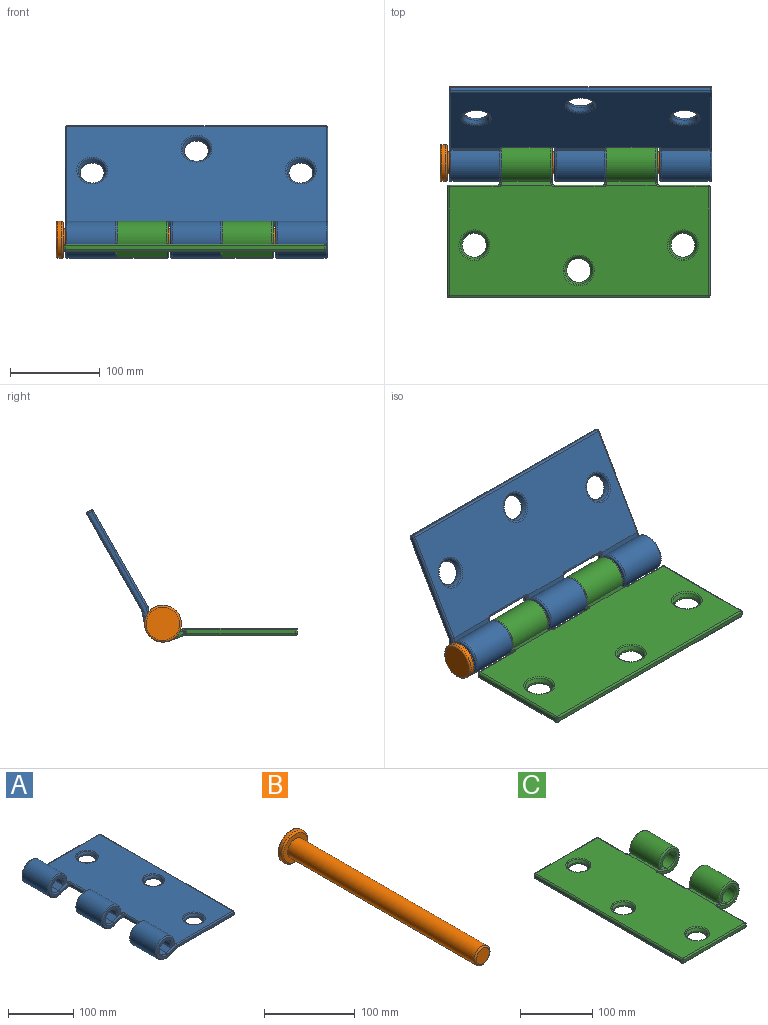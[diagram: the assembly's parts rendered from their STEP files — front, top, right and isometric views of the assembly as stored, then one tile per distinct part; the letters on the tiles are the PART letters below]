
ASSEMBLY  parts=3 mates=2
PART A: 101 faces, bbox 171.7x292x44.4 mm
  f0: cylinder r=12.5mm len=54.4mm, axis (0,1,0), area 3703.3mm2, adj f2,f8,f36,f85
  f1: cylinder r=12.5mm len=54.4mm, axis (0,1,0), area 3703.3mm2, adj f3,f9,f45,f56
  f2: plane 55.3x20.54mm, normal (-0.32,0,0.95), area 1179mm2, adj f0,f12,f33,f34,f35,f80
  f3: plane 56.21x20.54mm, normal (-0.32,0,0.95), area 1179.8mm2, adj f1,f12,f39,f41,f43,f53,f54,f55
  f4: plane 54.63x17.59mm, normal (0.34,0,-0.94), area 1016.4mm2, adj f6,f14,f42,f44,f93
  f5: plane 54.85x17.59mm, normal (0.34,0,-0.94), area 1016.5mm2, adj f7,f14,f51,f52,f62,f64
  f6: cylinder r=20.5mm len=54.4mm, axis (0,1,0), area 5913.6mm2, adj f4,f8,f40,f91
  f7: cylinder r=20.5mm len=54.4mm, axis (0,1,0), area 5913.6mm2, adj f5,f9,f49,f60
  f8: plane 54.4x8.42mm, normal (0,0,-1), area 458.3mm2, adj f0,f6,f38,f88
  f9: plane 54.4x8.42mm, normal (0,0,-1), area 458.3mm2, adj f1,f7,f47,f58
  f10: cylinder r=12.5mm len=54.4mm, axis (0,1,0), area 3703.3mm2, adj f11,f17,f65,f73
  f11: plane 55.3x20.54mm, normal (-0.32,0,0.95), area 1179mm2, adj f10,f12,f59,f61,f63,f74
  f12: plane 288x123mm, normal (0,0,1), area 32386.8mm2, adj f2,f3,f11,f35,f37,f39,f55,f57
  f13: plane 288x4mm, normal (1,0,0), area 1152mm2, adj f82,f83,f89,f90
  f14: plane 288x123.06mm, normal (0,0,-1), area 32998.9mm2, adj f4,f5,f15,f44,f46,f48,f50,f52
  f15: plane 54.63x17.59mm, normal (0.34,0,-0.94), area 1016.4mm2, adj f14,f16,f71,f72,f79
  f16: cylinder r=20.5mm len=54.4mm, axis (0,1,0), area 5913.6mm2, adj f15,f17,f69,f77
  f17: plane 54.4x8.42mm, normal (0,0,-1), area 458.3mm2, adj f10,f16,f67,f75
  f18: plane 166x37mm, normal (0,-1,0), area 913.5mm2, adj f80,f81,f85,f88,f89,f91,f93,f94
  f19: plane 166x37mm, normal (0,1,0), area 913.5mm2, adj f73,f74,f75,f76,f77,f79,f83,f84
  f20: cone r=16mm half-angle=26.6deg, axis (0,0,1), area 406mm2, adj f99,f100
  f21: cone r=12mm half-angle=26.6deg, axis (0,0,1), area 406mm2, adj f97,f98
  f22: cone r=16mm half-angle=26.6deg, axis (0,0,1), area 406mm2, adj f95,f96
  f23: plane 54.4x4mm, normal (-1,0,0), area 217.6mm2, adj f29,f30,f57,f68
  f24: plane 41x37mm, normal (0,1,0), area 413.9mm2, adj f29,f54,f56,f58,f60,f62
  f25: plane 41x37mm, normal (0,-1,0), area 413.9mm2, adj f30,f63,f65,f67,f69,f71
  f26: plane 54.4x4mm, normal (-1,0,0), area 217.6mm2, adj f31,f32,f37,f48
  f27: plane 41x37mm, normal (0,1,0), area 413.9mm2, adj f31,f34,f36,f38,f40,f42
  f28: plane 41x37mm, normal (0,-1,0), area 413.9mm2, adj f32,f43,f45,f47,f49,f51
  f29: cylinder r=2mm len=4.59mm, axis (0,0,1), area 12.3mm2, adj f23,f24,f53,f55,f64,f66
  f30: cylinder r=2mm len=4.59mm, axis (0,0,-1), area 12.3mm2, adj f23,f25,f59,f61,f70,f72
  f31: cylinder r=2mm len=4.59mm, axis (0,0,1), area 12.3mm2, adj f26,f27,f33,f35,f44,f46
  f32: cylinder r=2mm len=4.59mm, axis (0,0,-1), area 12.3mm2, adj f26,f28,f39,f41,f50,f52
  f33: bspline ~2.75x2.54mm, area 6mm2, adj f2,f31,f34,f35
  f34: cylinder r=2mm len=18.54mm, axis (-0.95,0,-0.32), area 59.3mm2, adj f2,f27,f33,f36
  f35: torus R=4mm, axis (0,0,-1), area 8.7mm2, adj f2,f12,f31,f33,f37
  f36: torus R=14.5mm, axis (0,1,0), area 222mm2, adj f0,f27,f34,f38
  f37: cylinder r=2mm len=54.4mm, axis (0,-1,0), area 170.9mm2, adj f12,f26,f35,f39
  f38: cylinder r=2mm len=8.42mm, axis (1,0,0), area 19.6mm2, adj f8,f27,f36,f40
  f39: torus R=4mm, axis (0,0,-1), area 8.7mm2, adj f3,f12,f32,f37,f41
  f40: torus R=18.5mm, axis (0,1,0), area 326.9mm2, adj f6,f27,f38,f42
  f41: bspline ~3.65x3.11mm, area 6mm2, adj f3,f32,f39,f43
  f42: cylinder r=2mm len=16.94mm, axis (0.94,0,0.34), area 54.3mm2, adj f4,f27,f40,f44
  f43: cylinder r=2mm len=18.54mm, axis (0.95,0,0.32), area 59.3mm2, adj f3,f28,f41,f45
  f44: bspline ~2.47x2.33mm, area 3.5mm2, adj f4,f14,f31,f42,f46
  f45: torus R=14.5mm, axis (0,1,0), area 222mm2, adj f1,f28,f43,f47
  f46: torus R=4mm, axis (0,0,1), area 9.2mm2, adj f14,f31,f44,f48
  f47: cylinder r=2mm len=8.42mm, axis (-1,0,0), area 19.6mm2, adj f9,f28,f45,f49
  f48: cylinder r=2mm len=54.4mm, axis (0,1,0), area 170.9mm2, adj f14,f26,f46,f50
  f49: torus R=18.5mm, axis (0,1,0), area 326.9mm2, adj f7,f28,f47,f51
  f50: torus R=4mm, axis (0,0,1), area 9.2mm2, adj f14,f32,f48,f52
  f51: cylinder r=2mm len=16.94mm, axis (-0.94,0,-0.34), area 54.3mm2, adj f5,f28,f49,f52
  f52: bspline ~2.47x2.33mm, area 3.5mm2, adj f5,f14,f32,f50,f51
  f53: bspline ~2.75x2.54mm, area 6mm2, adj f3,f29,f54,f55
  f54: cylinder r=2mm len=18.54mm, axis (-0.95,0,-0.32), area 59.3mm2, adj f3,f24,f53,f56
  f55: torus R=4mm, axis (0,0,-1), area 8.7mm2, adj f3,f12,f29,f53,f57
  f56: torus R=14.5mm, axis (0,1,0), area 222mm2, adj f1,f24,f54,f58
  f57: cylinder r=2mm len=54.4mm, axis (0,-1,0), area 170.9mm2, adj f12,f23,f55,f59
  f58: cylinder r=2mm len=8.42mm, axis (1,0,0), area 19.6mm2, adj f9,f24,f56,f60
  f59: torus R=4mm, axis (0,0,-1), area 8.7mm2, adj f11,f12,f30,f57,f61
  f60: torus R=18.5mm, axis (0,1,0), area 326.9mm2, adj f7,f24,f58,f62
  f61: bspline ~3.65x3.11mm, area 6mm2, adj f11,f30,f59,f63
  f62: cylinder r=2mm len=16.94mm, axis (0.94,0,0.34), area 54.3mm2, adj f5,f24,f60,f64
  f63: cylinder r=2mm len=18.54mm, axis (0.95,0,0.32), area 59.3mm2, adj f11,f25,f61,f65
  f64: bspline ~2.47x2.33mm, area 3.5mm2, adj f5,f14,f29,f62,f66
  f65: torus R=14.5mm, axis (0,1,0), area 222mm2, adj f10,f25,f63,f67
  f66: torus R=4mm, axis (0,0,1), area 9.2mm2, adj f14,f29,f64,f68
  f67: cylinder r=2mm len=8.42mm, axis (-1,0,0), area 19.6mm2, adj f17,f25,f65,f69
  f68: cylinder r=2mm len=54.4mm, axis (0,1,0), area 170.9mm2, adj f14,f23,f66,f70
  f69: torus R=18.5mm, axis (0,1,0), area 326.9mm2, adj f16,f25,f67,f71
  f70: torus R=4mm, axis (0,0,1), area 9.2mm2, adj f14,f30,f68,f72
  f71: cylinder r=2mm len=16.94mm, axis (-0.94,0,-0.34), area 54.3mm2, adj f15,f25,f69,f72
  f72: bspline ~2.47x2.33mm, area 3.5mm2, adj f14,f15,f30,f70,f71
  f73: torus R=14.5mm, axis (0,-1,0), area 222mm2, adj f10,f19,f74,f75
  f74: cylinder r=2mm len=21.18mm, axis (0.95,0,0.32), area 67.5mm2, adj f11,f19,f73,f76
  f75: cylinder r=2mm len=8.42mm, axis (-1,0,0), area 19.6mm2, adj f17,f19,f73,f77
  f76: cylinder r=2mm len=123mm, axis (1,0,0), area 385.9mm2, adj f12,f19,f74,f78
  f77: torus R=18.5mm, axis (0,-1,0), area 326.9mm2, adj f16,f19,f75,f79
  f78: sphere r=2mm, area 6.3mm2, adj f76,f82,f83
  f79: cylinder r=2mm len=18.59mm, axis (-0.94,0,-0.34), area 59.2mm2, adj f15,f19,f77,f84
  f80: cylinder r=2mm len=21.18mm, axis (-0.95,0,-0.32), area 67.5mm2, adj f2,f18,f81,f85
  f81: cylinder r=2mm len=123mm, axis (-1,0,0), area 385.9mm2, adj f12,f18,f80,f86
  f82: cylinder r=2mm len=288mm, axis (0,1,0), area 904.8mm2, adj f12,f13,f78,f86
  f83: cylinder r=2mm len=4mm, axis (0,0,-1), area 12.6mm2, adj f13,f19,f78,f87
  f84: cylinder r=2mm len=123.35mm, axis (-1,0,0), area 387mm2, adj f14,f19,f79,f87
  f85: torus R=14.5mm, axis (0,-1,0), area 222mm2, adj f0,f18,f80,f88
  f86: sphere r=2mm, area 6.3mm2, adj f81,f82,f89
  f87: sphere r=2mm, area 4mm2, adj f83,f84,f90
  f88: cylinder r=2mm len=8.42mm, axis (1,0,0), area 19.6mm2, adj f8,f18,f85,f91
  f89: cylinder r=2mm len=4mm, axis (0,0,1), area 12.6mm2, adj f13,f18,f86,f92
  f90: cylinder r=2mm len=288mm, axis (0,1,0), area 904.8mm2, adj f13,f14,f87,f92
  f91: torus R=18.5mm, axis (0,-1,0), area 326.9mm2, adj f6,f18,f88,f93
  f92: sphere r=2mm, area 6.3mm2, adj f89,f90,f94
  f93: cylinder r=2mm len=18.59mm, axis (0.94,0,0.34), area 59.2mm2, adj f4,f18,f91,f94
  f94: cylinder r=2mm len=123.35mm, axis (1,0,0), area 387mm2, adj f14,f18,f92,f93
  f95: torus R=17.24mm, axis (0,0,-1), area 225.9mm2, adj f12,f22
  f96: torus R=15.24mm, axis (0,0,1), area 353.1mm2, adj f14,f22
  f97: torus R=15.24mm, axis (0,0,1), area 353.1mm2, adj f14,f21
  f98: torus R=17.24mm, axis (0,0,-1), area 225.9mm2, adj f12,f21
  f99: torus R=15.24mm, axis (0,0,1), area 353.1mm2, adj f14,f20
  f100: torus R=17.24mm, axis (0,0,-1), area 225.9mm2, adj f12,f20
PART B: 8 faces, bbox 44.4x300x44.4 mm
  f0: cylinder r=12.25mm len=290mm, axis (0,1,0), area 22321mm2, adj f4,f7
  f1: plane 20.5x20.5mm, normal (0,-1,0), area 330.1mm2, adj f7
  f2: cylinder r=20.5mm len=41mm, axis (0,-1,0), area 515.2mm2, adj f5,f6
  f3: plane 37x37mm, normal (0,1,0), area 1075.2mm2, adj f6
  f4: plane 37x37mm, normal (0,-1,0), area 603.8mm2, adj f0,f5
  f5: torus R=18.5mm, axis (0,1,0), area 390.3mm2, adj f2,f4
  f6: torus R=18.5mm, axis (0,1,0), area 390.3mm2, adj f2,f3
  f7: torus R=10.25mm, axis (0,1,0), area 227.5mm2, adj f0,f1
PART C: 95 faces, bbox 171.7x292x44.4 mm
  f0: cylinder r=12.5mm len=54.4mm, axis (0,1,0), area 3703.3mm2, adj f2,f8,f36,f60
  f1: cylinder r=12.5mm len=54.4mm, axis (0,1,0), area 3703.3mm2, adj f3,f9,f53,f69
  f2: plane 56.21x20.54mm, normal (0.32,0,0.95), area 1179.8mm2, adj f0,f12,f38,f40,f42,f57,f58,f59
  f3: plane 56.21x20.54mm, normal (0.32,0,0.95), area 1179.8mm2, adj f1,f12,f54,f55,f56,f63,f65,f67
  f4: plane 54.85x17.59mm, normal (-0.34,0,-0.94), area 1016.5mm2, adj f6,f14,f29,f30,f66,f68
  f5: plane 54.85x17.59mm, normal (-0.34,0,-0.94), area 1016.5mm2, adj f7,f14,f45,f47,f75,f76
  f6: cylinder r=20.5mm len=54.4mm, axis (0,1,0), area 5913.6mm2, adj f4,f8,f32,f64
  f7: cylinder r=20.5mm len=54.4mm, axis (0,1,0), area 5913.6mm2, adj f5,f9,f49,f73
  f8: plane 54.4x8.42mm, normal (0,0,-1), area 458.3mm2, adj f0,f6,f34,f62
  f9: plane 54.4x8.42mm, normal (0,0,-1), area 458.3mm2, adj f1,f7,f51,f71
  f10: plane 121x4mm, normal (0,-1,0), area 484mm2, adj f39,f50,f78,f84
  f11: plane 121x4mm, normal (0,1,0), area 484mm2, adj f35,f46,f81,f87
  f12: plane 288x123mm, normal (0,0,1), area 32278mm2, adj f2,f3,f42,f44,f46,f48,f50,f52
  f13: plane 288x4mm, normal (-1,0,0), area 1152mm2, adj f37,f48,f78,f81
  f14: plane 288x123.06mm, normal (0,0,-1), area 32890.1mm2, adj f4,f5,f29,f31,f33,f35,f37,f39
  f15: cone r=16mm half-angle=26.6deg, axis (0,0,1), area 406mm2, adj f93,f94
  f16: cone r=12mm half-angle=26.6deg, axis (0,0,1), area 406mm2, adj f91,f92
  f17: cone r=16mm half-angle=26.6deg, axis (0,0,1), area 406mm2, adj f89,f90
  f18: plane 54.4x4mm, normal (1,0,0), area 217.6mm2, adj f25,f41,f52,f84
  f19: plane 41x37mm, normal (0,-1,0), area 413.9mm2, adj f25,f47,f49,f51,f53,f55
  f20: plane 54.4x4mm, normal (1,0,0), area 217.6mm2, adj f26,f27,f61,f72
  f21: plane 41x37mm, normal (0,-1,0), area 413.9mm2, adj f26,f58,f60,f62,f64,f66
  f22: plane 41x37mm, normal (0,1,0), area 413.9mm2, adj f27,f67,f69,f71,f73,f75
  f23: plane 54.4x4mm, normal (1,0,0), area 217.6mm2, adj f28,f33,f44,f87
  f24: plane 41x37mm, normal (0,1,0), area 413.9mm2, adj f28,f30,f32,f34,f36,f38
  f25: cylinder r=2mm len=4.59mm, axis (0,0,-1), area 12.3mm2, adj f18,f19,f43,f45,f54,f56
  f26: cylinder r=2mm len=4.59mm, axis (0,0,-1), area 12.3mm2, adj f20,f21,f57,f59,f68,f70
  f27: cylinder r=2mm len=4.59mm, axis (0,0,1), area 12.3mm2, adj f20,f22,f63,f65,f74,f76
  f28: cylinder r=2mm len=4.59mm, axis (0,0,1), area 12.3mm2, adj f23,f24,f29,f31,f40,f42
  f29: bspline ~2.47x2.33mm, area 3.5mm2, adj f4,f14,f28,f30,f31
  f30: cylinder r=2mm len=16.94mm, axis (0.94,0,-0.34), area 54.3mm2, adj f4,f24,f29,f32
  f31: torus R=4mm, axis (0,0,1), area 9.2mm2, adj f14,f28,f29,f33
  f32: torus R=18.5mm, axis (0,-1,0), area 326.9mm2, adj f6,f24,f30,f34
  f33: cylinder r=2mm len=54.4mm, axis (0,-1,0), area 170.9mm2, adj f14,f23,f31,f88
  f34: cylinder r=2mm len=8.42mm, axis (1,0,0), area 19.6mm2, adj f8,f24,f32,f36
  f35: cylinder r=2mm len=121mm, axis (1,0,0), area 380.1mm2, adj f11,f14,f80,f88
  f36: torus R=14.5mm, axis (0,-1,0), area 222mm2, adj f0,f24,f34,f38
  f37: cylinder r=2mm len=288mm, axis (0,1,0), area 904.8mm2, adj f13,f14,f77,f80
  f38: cylinder r=2mm len=18.54mm, axis (-0.95,0,0.32), area 59.3mm2, adj f2,f24,f36,f40
  f39: cylinder r=2mm len=121mm, axis (-1,0,0), area 380.1mm2, adj f10,f14,f77,f85
  f40: bspline ~3.65x3.11mm, area 6mm2, adj f2,f28,f38,f42
  f41: cylinder r=2mm len=54.4mm, axis (0,-1,0), area 170.9mm2, adj f14,f18,f43,f85
  f42: torus R=4mm, axis (0,0,-1), area 8.7mm2, adj f2,f12,f28,f40,f44
  f43: torus R=4mm, axis (0,0,1), area 9.2mm2, adj f14,f25,f41,f45
  f44: cylinder r=2mm len=54.4mm, axis (0,1,0), area 170.9mm2, adj f12,f23,f42,f86
  f45: bspline ~2.47x2.33mm, area 3.5mm2, adj f5,f14,f25,f43,f47
  f46: cylinder r=2mm len=121mm, axis (-1,0,0), area 380.1mm2, adj f11,f12,f82,f86
  f47: cylinder r=2mm len=16.94mm, axis (-0.94,0,0.34), area 54.3mm2, adj f5,f19,f45,f49
  f48: cylinder r=2mm len=288mm, axis (0,1,0), area 904.8mm2, adj f12,f13,f79,f82
  f49: torus R=18.5mm, axis (0,-1,0), area 326.9mm2, adj f7,f19,f47,f51
  f50: cylinder r=2mm len=121mm, axis (1,0,0), area 380.1mm2, adj f10,f12,f79,f83
  f51: cylinder r=2mm len=8.42mm, axis (-1,0,0), area 19.6mm2, adj f9,f19,f49,f53
  f52: cylinder r=2mm len=54.4mm, axis (0,-1,0), area 170.9mm2, adj f12,f18,f54,f83
  f53: torus R=14.5mm, axis (0,-1,0), area 222mm2, adj f1,f19,f51,f55
  f54: torus R=4mm, axis (0,0,-1), area 8.7mm2, adj f3,f12,f25,f52,f56
  f55: cylinder r=2mm len=18.54mm, axis (0.95,0,-0.32), area 59.3mm2, adj f3,f19,f53,f56
  f56: bspline ~3.65x3.11mm, area 6mm2, adj f3,f25,f54,f55
  f57: bspline ~3.65x3.11mm, area 6mm2, adj f2,f26,f58,f59
  f58: cylinder r=2mm len=18.54mm, axis (0.95,0,-0.32), area 59.3mm2, adj f2,f21,f57,f60
  f59: torus R=4mm, axis (0,0,-1), area 8.7mm2, adj f2,f12,f26,f57,f61
  f60: torus R=14.5mm, axis (0,-1,0), area 222mm2, adj f0,f21,f58,f62
  f61: cylinder r=2mm len=54.4mm, axis (0,1,0), area 170.9mm2, adj f12,f20,f59,f63
  f62: cylinder r=2mm len=8.42mm, axis (-1,0,0), area 19.6mm2, adj f8,f21,f60,f64
  f63: torus R=4mm, axis (0,0,-1), area 8.7mm2, adj f3,f12,f27,f61,f65
  f64: torus R=18.5mm, axis (0,-1,0), area 326.9mm2, adj f6,f21,f62,f66
  f65: bspline ~2.75x2.54mm, area 6mm2, adj f3,f27,f63,f67
  f66: cylinder r=2mm len=16.94mm, axis (-0.94,0,0.34), area 54.3mm2, adj f4,f21,f64,f68
  f67: cylinder r=2mm len=18.54mm, axis (-0.95,0,0.32), area 59.3mm2, adj f3,f22,f65,f69
  f68: bspline ~2.47x2.33mm, area 3.5mm2, adj f4,f14,f26,f66,f70
  f69: torus R=14.5mm, axis (0,-1,0), area 222mm2, adj f1,f22,f67,f71
  f70: torus R=4mm, axis (0,0,1), area 9.2mm2, adj f14,f26,f68,f72
  f71: cylinder r=2mm len=8.42mm, axis (1,0,0), area 19.6mm2, adj f9,f22,f69,f73
  f72: cylinder r=2mm len=54.4mm, axis (0,-1,0), area 170.9mm2, adj f14,f20,f70,f74
  f73: torus R=18.5mm, axis (0,-1,0), area 326.9mm2, adj f7,f22,f71,f75
  f74: torus R=4mm, axis (0,0,1), area 9.2mm2, adj f14,f27,f72,f76
  f75: cylinder r=2mm len=16.94mm, axis (0.94,0,-0.34), area 54.3mm2, adj f5,f22,f73,f76
  f76: bspline ~2.47x2.33mm, area 3.5mm2, adj f5,f14,f27,f74,f75
  f77: sphere r=2mm, area 6.3mm2, adj f37,f39,f78
  f78: cylinder r=2mm len=4mm, axis (0,0,1), area 12.6mm2, adj f10,f13,f77,f79
  f79: sphere r=2mm, area 6.3mm2, adj f48,f50,f78
  f80: sphere r=2mm, area 8.6mm2, adj f35,f37,f81
  f81: cylinder r=2mm len=4mm, axis (0,0,-1), area 12.6mm2, adj f11,f13,f80,f82
  f82: sphere r=2mm, area 6.3mm2, adj f46,f48,f81
  f83: sphere r=2mm, area 6.3mm2, adj f50,f52,f84
  f84: cylinder r=2mm len=4mm, axis (0,0,1), area 12.6mm2, adj f10,f18,f83,f85
  f85: sphere r=2mm, area 6.3mm2, adj f39,f41,f84
  f86: sphere r=2mm, area 4mm2, adj f44,f46,f87
  f87: cylinder r=2mm len=4mm, axis (0,0,-1), area 12.6mm2, adj f11,f23,f86,f88
  f88: sphere r=2mm, area 6.3mm2, adj f33,f35,f87
  f89: torus R=15.24mm, axis (0,0,1), area 353.1mm2, adj f14,f17
  f90: torus R=17.24mm, axis (0,0,-1), area 225.9mm2, adj f12,f17
  f91: torus R=17.24mm, axis (0,0,-1), area 225.9mm2, adj f12,f16
  f92: torus R=15.24mm, axis (0,0,1), area 353.1mm2, adj f14,f16
  f93: torus R=15.24mm, axis (0,0,1), area 353.1mm2, adj f14,f15
  f94: torus R=17.24mm, axis (0,0,-1), area 225.9mm2, adj f12,f15
PLACE A rot(axis=(0.45,-0.45,0.77),104.6deg) t=(-290,-7.83,-23.75)mm
PLACE B rot(axis=(0,0,1),90deg) t=(-292,-24.5,-5)mm
PLACE C rot(axis=(0,0,1),90deg) t=(-292,-24.5,-5)mm
MATE revolute A.f0 <-> C.f0  axis (1,0,0) through (-114.8,0,0)mm
MATE revolute A.f0 <-> B.f0  axis (1,0,0) through (0,0,0)mm
